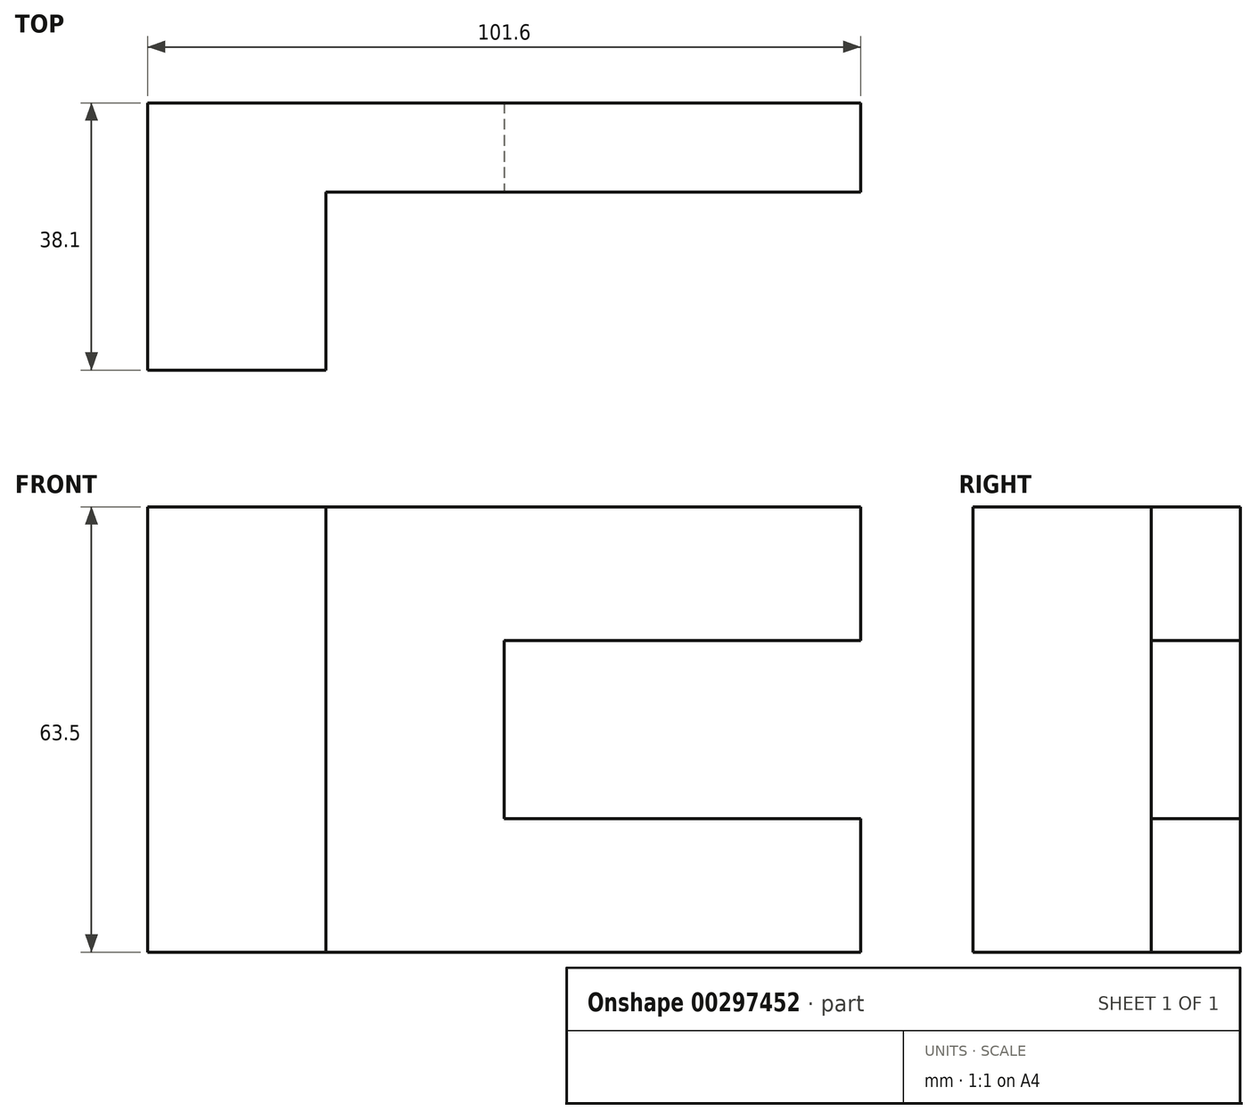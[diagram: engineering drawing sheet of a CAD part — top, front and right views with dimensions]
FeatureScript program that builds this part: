
annotation { "Feature Type Name" : "Feature", "Feature Type Description" : "" }
export const myFeature = defineFeature(function(context is Context, id is Id, definition is map)
    precondition{}
    {
        {
            var Q0;
            Q0=qCreatedBy(makeId("Front.planeOp"),FACE);
            var sketch = newSketch(context, id + "F0", { "sketchPlane" : qUnion([Q0])});
            skLineSegment(sketch, "E0.bottom", {"start": v(50.8, 31.75) * mm, "end": v(-50.8, 31.75) * mm});
            skLineSegment(sketch, "E0.top", {"start": v(50.8, -31.75) * mm, "end": v(-50.8, -31.75) * mm});
            skLineSegment(sketch, "E0.left", {"start": v(50.8, 31.75) * mm, "end": v(50.8, -31.75) * mm});
            skLineSegment(sketch, "E0.right", {"start": v(-50.8, 31.75) * mm, "end": v(-50.8, -31.75) * mm});
            skPoint(sketch, "E0.middle", {"position": v(0, 0) * mm});
            skSolve(sketch);
        }
        {
            var Q0;
            Q0 = qSketchRegion(id + "F0", true);
            extrude(context, id + "F1", {"entities" : qUnion([Q0]), "depth" : 38.1 * mm});
        }
        {
            var Q0;
            Q0=makeQuery(id+"F1.opExtrude","CAP_FACE",FACE,{"disambiguationData":[OSD([sQuery(id+"F0.wireOp",EDGE,"E0.bottom"),sQuery(id+"F0.wireOp",EDGE,"E0.top"),sQuery(id+"F0.wireOp",EDGE,"E0.left"),sQuery(id+"F0.wireOp",EDGE,"E0.right")])],"isStart":false});
            var sketch = newSketch(context, id + "F2", { "sketchPlane" : qUnion([Q0])});
            skLineSegment(sketch, "E1.bottom", {"start": v(50.8, 12.7) * mm, "end": v(0, 12.7) * mm});
            skLineSegment(sketch, "E1.top", {"start": v(50.8, -12.7) * mm, "end": v(0, -12.7) * mm});
            skLineSegment(sketch, "E1.left", {"start": v(50.8, 12.7) * mm, "end": v(50.8, -12.7) * mm});
            skLineSegment(sketch, "E1.right", {"start": v(0, 12.7) * mm, "end": v(0, -12.7) * mm});
            skSolve(sketch);
        }
        {
            var Q0;
            Q0 = qSketchRegion(id + "F2", true);
            extrude(context, id + "F3", {"entities" : qUnion([Q0]), "operationType" : NewBodyOperationType.REMOVE, "endBound" : BoundingType.THROUGH_ALL, "oppositeDirection" : true, "depth" : 25.4 * mm});
        }
        {
            var Q0;
            Q0=makeQuery(id+"F1.opExtrude","CAP_FACE",FACE,{"disambiguationData":[OSD([sQuery(id+"F0.wireOp",EDGE,"E0.bottom"),sQuery(id+"F0.wireOp",EDGE,"E0.top"),sQuery(id+"F0.wireOp",EDGE,"E0.left"),sQuery(id+"F0.wireOp",EDGE,"E0.right")])],"isStart":false});
            var sketch = newSketch(context, id + "F4", { "sketchPlane" : qUnion([Q0])});
            skLineSegment(sketch, "E2.bottom", {"start": v(50.8, 31.75) * mm, "end": v(-25.4, 31.75) * mm});
            skLineSegment(sketch, "E2.top", {"start": v(50.8, -31.75) * mm, "end": v(-25.4, -31.75) * mm});
            skLineSegment(sketch, "E2.left", {"start": v(50.8, 31.75) * mm, "end": v(50.8, -31.75) * mm});
            skLineSegment(sketch, "E2.right", {"start": v(-25.4, 31.75) * mm, "end": v(-25.4, -31.75) * mm});
            skSolve(sketch);
        }
        {
            var Q0;
            Q0 = qSketchRegion(id + "F4", true);
            extrude(context, id + "F5", {"entities" : qUnion([Q0]), "operationType" : NewBodyOperationType.REMOVE, "oppositeDirection" : true, "depth" : 25.4 * mm});
        }
    });
